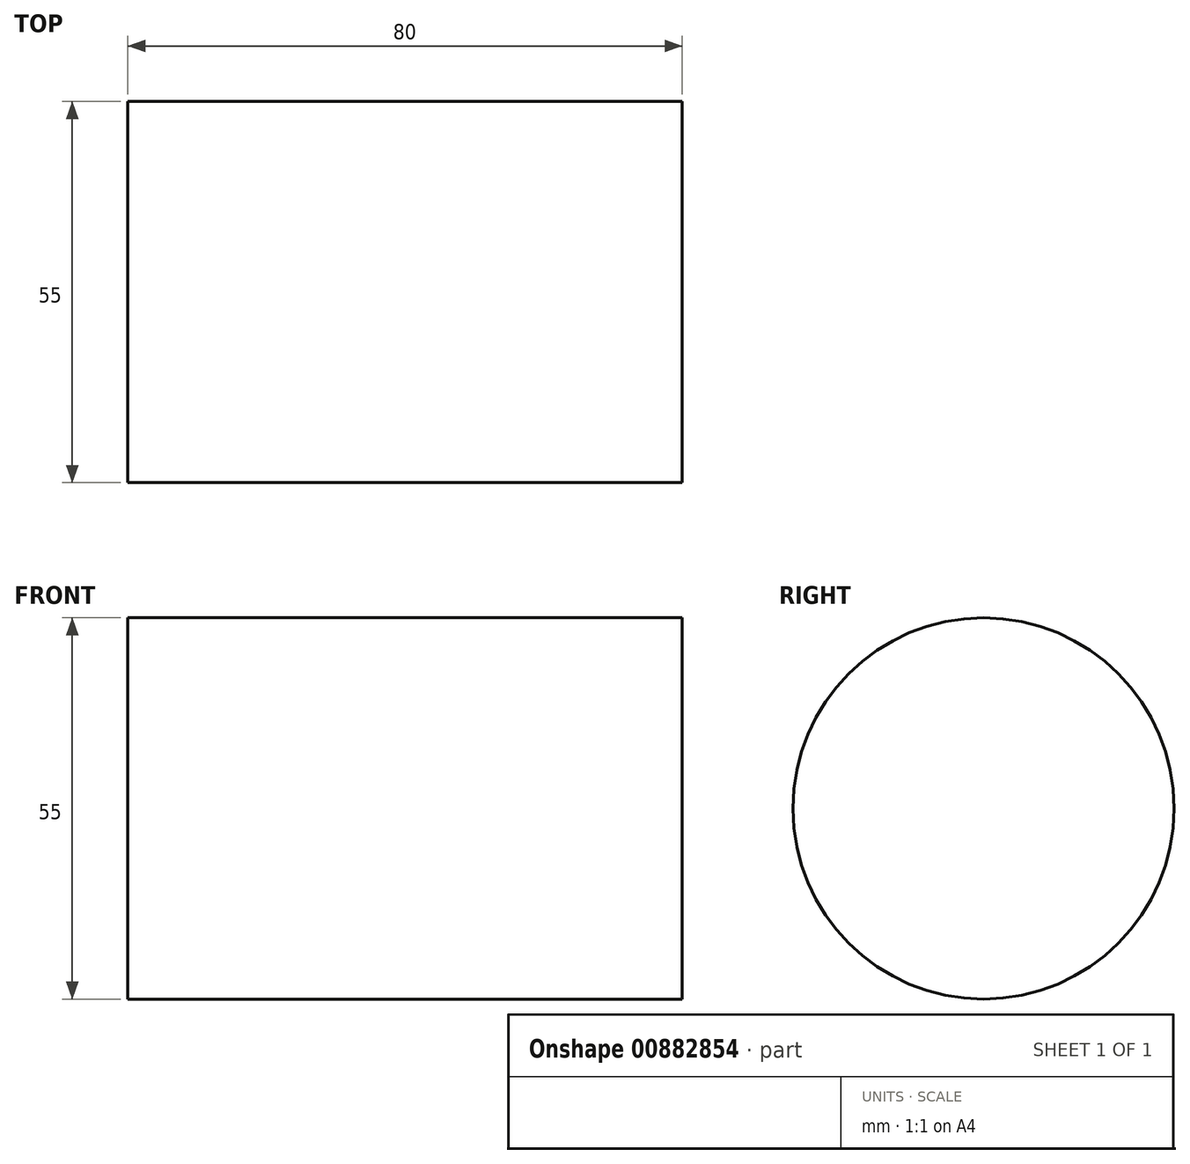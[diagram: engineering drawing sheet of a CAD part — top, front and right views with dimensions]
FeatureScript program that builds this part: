
annotation { "Feature Type Name" : "Feature", "Feature Type Description" : "" }
export const myFeature = defineFeature(function(context is Context, id is Id, definition is map)
    precondition{}
    {
        {
            var Q0;
            Q0=qCreatedBy(makeId("Right.planeOp"),FACE);
            var sketch = newSketch(context, id + "F0", { "sketchPlane" : qUnion([Q0])});
            skCircle(sketch, "E0", {"center": v(0, 0) * mm, "radius": 27.5 * mm});
            skSolve(sketch);
        }
        {
            var Q0;
            Q0 = qSketchRegion(id + "F0", true);
            extrude(context, id + "F1", {"entities" : qUnion([Q0]), "depth" : 80 * mm, "offsetDistance" : 25 * mm});
        }
    });
